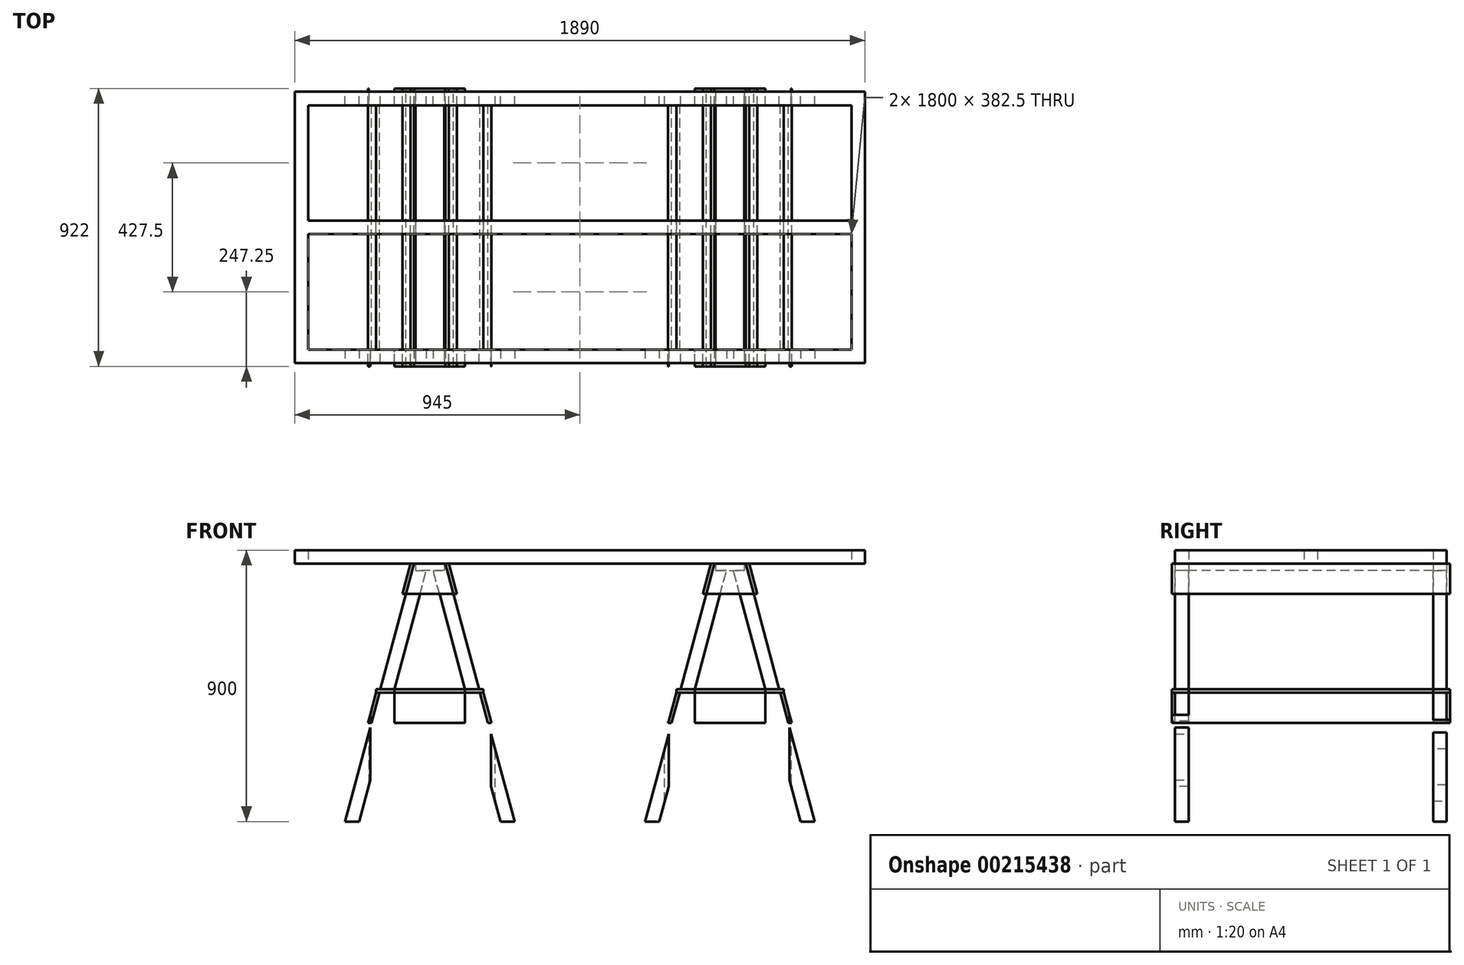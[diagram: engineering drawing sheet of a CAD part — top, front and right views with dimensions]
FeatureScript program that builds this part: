
annotation { "Feature Type Name" : "Feature", "Feature Type Description" : "" }
export const myFeature = defineFeature(function(context is Context, id is Id, definition is map)
    precondition{}
    {
        {
            var Q0;
            Q0=qCreatedBy(makeId("Top.planeOp"),FACE);
            var sketch = newSketch(context, id + "F0", { "sketchPlane" : qUnion([Q0])});
            skLineSegment(sketch, "E0.bottom", {"start": v(945, -450) * mm, "end": v(-945, -450) * mm});
            skLineSegment(sketch, "E0.top", {"start": v(945, 450) * mm, "end": v(-945, 450) * mm});
            skLineSegment(sketch, "E0.left", {"start": v(945, -450) * mm, "end": v(945, 450) * mm});
            skLineSegment(sketch, "E0.right", {"start": v(-945, -450) * mm, "end": v(-945, 450) * mm});
            skLineSegment(sketch, "E1.0", {"start": v(900, 405) * mm, "end": v(-900, 405) * mm});
            skLineSegment(sketch, "E1.1", {"start": v(900, -405) * mm, "end": v(900, 405) * mm});
            skLineSegment(sketch, "E1.2", {"start": v(900, -405) * mm, "end": v(-900, -405) * mm});
            skLineSegment(sketch, "E1.3", {"start": v(-900, -405) * mm, "end": v(-900, 405) * mm});
            skLineSegment(sketch, "E2.bottom", {"start": v(900, -22.5) * mm, "end": v(-900, -22.5) * mm});
            skLineSegment(sketch, "E2.top", {"start": v(900, 22.5) * mm, "end": v(-900, 22.5) * mm});
            skLineSegment(sketch, "E2.left", {"start": v(900, -22.5) * mm, "end": v(900, 22.5) * mm});
            skLineSegment(sketch, "E2.right", {"start": v(-900, -22.5) * mm, "end": v(-900, 22.5) * mm});
            skLineSegment(sketch, "E3.bottom", {"start": v(-320, 405) * mm, "end": v(-275, 405) * mm});
            skLineSegment(sketch, "E3.top", {"start": v(-320, -405) * mm, "end": v(-275, -405) * mm});
            skLineSegment(sketch, "E3.left", {"start": v(-320, 405) * mm, "end": v(-320, -405) * mm});
            skLineSegment(sketch, "E3.right", {"start": v(-275, 405) * mm, "end": v(-275, -405) * mm});
            skLineSegment(sketch, "E4.bottom", {"start": v(275, 405) * mm, "end": v(320, 405) * mm});
            skLineSegment(sketch, "E4.top", {"start": v(275, -405) * mm, "end": v(320, -405) * mm});
            skLineSegment(sketch, "E4.left", {"start": v(275, 405) * mm, "end": v(275, -405) * mm});
            skLineSegment(sketch, "E4.right", {"start": v(320, 405) * mm, "end": v(320, -405) * mm});
            skLineSegment(sketch, "E5", {"start": v(-297.5, 556.74) * mm, "end": v(-297.5, -663.13) * mm, "construction": true});
            skLineSegment(sketch, "E6", {"start": v(297.5, 521.89) * mm, "end": v(297.5, -577.16) * mm, "construction": true});
            skLineSegment(sketch, "E7", {"start": v(0, 0) * mm, "end": v(-1247.86, 0) * mm, "construction": true});
            skLineSegment(sketch, "E8", {"start": v(0, 0) * mm, "end": v(0, -826.24) * mm, "construction": true});
            skPoint(sketch, "E8.endSnap0", {"position": v(0, -405) * mm});
            skSolve(sketch);
        }
        {
            var Q0;
            Q0 = qSketchRegion(id + "F0", true);
            var Q1;
            {var subQ5=sQuery(id+"F0.wireOp",EDGE,"E3.bottom");Q1=makeQuery(id+"F0.imprint","IMPRINT",FACE,{"disambiguationData":[TD([[makeQuery(id+"F0.imprint","IMPRINT",EDGE,{"derivedFrom":subQ5}),-1.0]])]});}
            var Q2;
            {var subQ0=sQuery(id+"F0.wireOp",EDGE,"E2.right");Q2=makeQuery(id+"F0.imprint","IMPRINT",FACE,{"disambiguationData":[TD([[makeQuery(id+"F0.imprint","IMPRINT",EDGE,{"derivedFrom":subQ0}),-1.0]])]});}
            var Q3;
            {var subQ0=sQuery(id+"F0.wireOp",EDGE,"E3.right");var subQ1=sQuery(id+"F0.wireOp",EDGE,"E2.bottom");var subQ2=makeQuery(id+"F0.imprint","INTERSECT",VERTEX,{"derivedFrom":[subQ1,subQ0]});Q3=makeQuery(id+"F0.imprint","IMPRINT",FACE,{"disambiguationData":[TD([[makeQuery(id+"F0.imprint","IMPRINT",EDGE,{"disambiguationData":[TD([[subQ2,-1.0]])],"derivedFrom":subQ1}),-1.0]])]});}
            var Q4;
            {var subQ5=sQuery(id+"F0.wireOp",EDGE,"E3.top");Q4=makeQuery(id+"F0.imprint","IMPRINT",FACE,{"disambiguationData":[TD([[makeQuery(id+"F0.imprint","IMPRINT",EDGE,{"derivedFrom":subQ5}),1.0]])]});}
            var Q5;
            {var subQ0=sQuery(id+"F0.wireOp",EDGE,"EqetSjWE-wR77-RckO-4Gww-h4ygaoZgAjXq.right");var subQ1=sQuery(id+"F0.wireOp",EDGE,"E2.bottom");var subQ2=makeQuery(id+"F0.imprint","INTERSECT",VERTEX,{"derivedFrom":[subQ1,subQ0]});Q5=makeQuery(id+"F0.imprint","IMPRINT",FACE,{"disambiguationData":[TD([[makeQuery(id+"F0.imprint","IMPRINT",EDGE,{"disambiguationData":[TD([[subQ2,-1.0]])],"derivedFrom":subQ1}),-1.0]])]});}
            var Q6;
            {var subQ5=sQuery(id+"F0.wireOp",EDGE,"EqetSjWE-wR77-RckO-4Gww-h4ygaoZgAjXq.top");Q6=makeQuery(id+"F0.imprint","IMPRINT",FACE,{"disambiguationData":[TD([[makeQuery(id+"F0.imprint","IMPRINT",EDGE,{"derivedFrom":subQ5}),1.0]])]});}
            var Q7;
            {var subQ0=sQuery(id+"F0.wireOp",EDGE,"E4.left");var subQ1=sQuery(id+"F0.wireOp",EDGE,"E2.bottom");var subQ2=makeQuery(id+"F0.imprint","INTERSECT",VERTEX,{"derivedFrom":[subQ1,subQ0]});Q7=makeQuery(id+"F0.imprint","IMPRINT",FACE,{"disambiguationData":[TD([[makeQuery(id+"F0.imprint","IMPRINT",EDGE,{"disambiguationData":[TD([[subQ2,-1.0]])],"derivedFrom":subQ1}),-1.0]])]});}
            var Q8;
            {var subQ5=sQuery(id+"F0.wireOp",EDGE,"E4.bottom");Q8=makeQuery(id+"F0.imprint","IMPRINT",FACE,{"disambiguationData":[TD([[makeQuery(id+"F0.imprint","IMPRINT",EDGE,{"derivedFrom":subQ5}),-1.0]])]});}
            var Q9;
            {var subQ0=sQuery(id+"F0.wireOp",EDGE,"E2.left");Q9=makeQuery(id+"F0.imprint","IMPRINT",FACE,{"disambiguationData":[TD([[makeQuery(id+"F0.imprint","IMPRINT",EDGE,{"derivedFrom":subQ0}),1.0]])]});}
            var Q10;
            {var subQ5=sQuery(id+"F0.wireOp",EDGE,"E4.top");Q10=makeQuery(id+"F0.imprint","IMPRINT",FACE,{"disambiguationData":[TD([[makeQuery(id+"F0.imprint","IMPRINT",EDGE,{"derivedFrom":subQ5}),1.0]])]});}
            var Q11;
            {var subQ0=sQuery(id+"F0.wireOp",EDGE,"E4.right");var subQ1=sQuery(id+"F0.wireOp",EDGE,"E2.bottom");var subQ2=makeQuery(id+"F0.imprint","INTERSECT",VERTEX,{"derivedFrom":[subQ1,subQ0]});Q11=makeQuery(id+"F0.imprint","IMPRINT",FACE,{"disambiguationData":[TD([[makeQuery(id+"F0.imprint","IMPRINT",EDGE,{"disambiguationData":[TD([[subQ2,-1.0]])],"derivedFrom":subQ1}),-1.0]])]});}
            var Q12;
            {var subQ5=sQuery(id+"F0.wireOp",EDGE,"EqetSjWE-wR77-RckO-4Gww-h4ygaoZgAjXq.bottom");Q12=makeQuery(id+"F0.imprint","IMPRINT",FACE,{"disambiguationData":[TD([[makeQuery(id+"F0.imprint","IMPRINT",EDGE,{"derivedFrom":subQ5}),-1.0]])]});}
            var Q13;
            {var subQ0=sQuery(id+"F0.wireOp",EDGE,"EqetSjWE-wR77-RckO-4Gww-h4ygaoZgAjXq.left");var subQ1=sQuery(id+"F0.wireOp",EDGE,"E2.bottom");var subQ2=makeQuery(id+"F0.imprint","INTERSECT",VERTEX,{"derivedFrom":[subQ1,subQ0]});Q13=makeQuery(id+"F0.imprint","IMPRINT",FACE,{"disambiguationData":[TD([[makeQuery(id+"F0.imprint","IMPRINT",EDGE,{"disambiguationData":[TD([[subQ2,-1.0]])],"derivedFrom":subQ1}),-1.0]])]});}
            extrude(context, id + "F1", {"entities" : qUnion([Q0, Q1, Q2, Q3, Q4, Q5, Q6, Q7, Q8, Q9, Q10, Q11, Q12, Q13]), "depth" : 45 * mm});
        }
        {
            var Q0;
            Q0=makeQuery(id+"F1.opExtrude","SWEPT_FACE",FACE,{"disambiguationData":[OSD([sQuery(id+"F0.wireOp",EDGE,"E0.bottom")])]});
            var sketch = newSketch(context, id + "F2", { "sketchPlane" : qUnion([Q0])});
            skLineSegment(sketch, "E9.bottom", {"start": v(-545, 0) * mm, "end": v(-450, 0) * mm});
            skLineSegment(sketch, "E9.top", {"start": v(-545, -22) * mm, "end": v(-450, -22) * mm});
            skLineSegment(sketch, "E9.left", {"start": v(-545, 0) * mm, "end": v(-545, -22) * mm});
            skLineSegment(sketch, "E9.right", {"start": v(-450, 0) * mm, "end": v(-450, -22) * mm});
            skPoint(sketch, "E10.endSnap0", {"position": v(-297.5, 22.5) * mm});
            skSolve(sketch);
        }
        {
            var Q0;
            Q0 = qSketchRegion(id + "F2", true);
            var Q1;
            Q1=makeQuery(id+"F1.opExtrude","SWEPT_FACE",FACE,{"disambiguationData":[OSD([sQuery(id+"F0.wireOp",EDGE,"E0.top")])]});
            extrude(context, id + "F3", {"entities" : qUnion([Q0]), "endBound" : BoundingType.UP_TO_SURFACE, "oppositeDirection" : true, "endBoundEntityFace" : qUnion([Q1]), "depth" : 25 * mm});
        }
        {
            var Q0;
            Q0=makeQuery(id+"F3.opExtrude","CAP_FACE",FACE,{"disambiguationData":[OSD([sQuery(id+"F2.wireOp",EDGE,"E9.bottom"),sQuery(id+"F2.wireOp",EDGE,"E9.top"),sQuery(id+"F2.wireOp",EDGE,"E9.left"),sQuery(id+"F2.wireOp",EDGE,"E9.right")])],"isStart":true});
            var sketch = newSketch(context, id + "F4", { "sketchPlane" : qUnion([Q0])});
            skLineSegment(sketch, "E11", {"start": v(-497.5, 134.53) * mm, "end": v(-497.5, -899.08) * mm, "construction": true});
            skPoint(sketch, "E11.startSnap0", {"position": v(-497.5, -22) * mm});
            skLineSegment(sketch, "E12", {"start": v(-549.48, 0) * mm, "end": v(-778.58, -855) * mm});
            skLineSegment(sketch, "E13", {"start": v(-778.58, -855) * mm, "end": v(-732, -855) * mm});
            skLineSegment(sketch, "E14", {"start": v(-732, -855) * mm, "end": v(-508.8, -22) * mm});
            skLineSegment(sketch, "E15", {"start": v(-508.8, -22) * mm, "end": v(-545, -22) * mm});
            skLineSegment(sketch, "E16", {"start": v(-545, -22) * mm, "end": v(-545, 0) * mm});
            skLineSegment(sketch, "E17.MirrorCS", {"start": v(-450, -22) * mm, "end": v(-450, 0) * mm});
            skLineSegment(sketch, "E18.MirrorCS", {"start": v(-486.2, -22) * mm, "end": v(-450, -22) * mm});
            skLineSegment(sketch, "E19.MirrorCS", {"start": v(-216.42, -855) * mm, "end": v(-263, -855) * mm});
            skLineSegment(sketch, "E20.MirrorCS", {"start": v(-445.52, 0) * mm, "end": v(-216.42, -855) * mm});
            skLineSegment(sketch, "E21.MirrorCS", {"start": v(-263, -855) * mm, "end": v(-486.2, -22) * mm});
            skLineSegment(sketch, "E22", {"start": v(-545, 0) * mm, "end": v(-549.48, 0) * mm});
            skLineSegment(sketch, "E23", {"start": v(-450, 0) * mm, "end": v(-445.52, 0) * mm});
            skPoint(sketch, "E24.orphan", {"position": v(-545, 16.74) * mm});
            skPoint(sketch, "E25.orphan", {"position": v(-450, 16.74) * mm});
            skSolve(sketch);
        }
        {
            var Q0;
            Q0 = qSketchRegion(id + "F4", true);
            extrude(context, id + "F5", {"entities" : qUnion([Q0]), "oppositeDirection" : true, "depth" : 45 * mm});
        }
        {
            var Q0;
            Q0=makeQuery(id+"F5.opExtrude","CAP_FACE",FACE,{"disambiguationData":[OSD([sQuery(id+"F4.wireOp",EDGE,"E12"),sQuery(id+"F4.wireOp",EDGE,"E13"),sQuery(id+"F4.wireOp",EDGE,"E14"),sQuery(id+"F4.wireOp",EDGE,"E15"),sQuery(id+"F4.wireOp",EDGE,"E16"),sQuery(id+"F4.wireOp",EDGE,"E22")])],"isStart":true});
            var sketch = newSketch(context, id + "F6", { "sketchPlane" : qUnion([Q0])});
            skLineSegment(sketch, "E26", {"start": v(-664.03, -427.5) * mm, "end": v(-330.97, -427.5) * mm});
            skPoint(sketch, "E26.endSnap0", {"position": v(-664.03, -427.5) * mm});
            skLineSegment(sketch, "E27", {"start": v(-330.97, -427.5) * mm, "end": v(-304.17, -527.5) * mm});
            skLineSegment(sketch, "E28", {"start": v(-304.17, -527.5) * mm, "end": v(-690.83, -527.5) * mm});
            skLineSegment(sketch, "E29", {"start": v(-690.83, -527.5) * mm, "end": v(-664.03, -427.5) * mm});
            skLineSegment(sketch, "E30", {"start": v(-549.48, 0) * mm, "end": v(-445.52, 0) * mm});
            skLineSegment(sketch, "E31", {"start": v(-445.52, 0) * mm, "end": v(-418.72, -100) * mm});
            skLineSegment(sketch, "E32", {"start": v(-418.72, -100) * mm, "end": v(-576.28, -100) * mm});
            skLineSegment(sketch, "E33", {"start": v(-576.28, -100) * mm, "end": v(-549.48, 0) * mm});
            skSolve(sketch);
        }
        {
            var Q0;
            Q0 = qSketchRegion(id + "F6", true);
            extrude(context, id + "F7", {"entities" : qUnion([Q0]), "depth" : 11 * mm});
        }
        {
            var Q0;
            Q0=makeQuery(id+"F5.opExtrude","SWEPT_BODY",BODY,{"disambiguationData":[OSD([sQuery(id+"F4.wireOp",EDGE,"E12"),sQuery(id+"F4.wireOp",EDGE,"E13"),sQuery(id+"F4.wireOp",EDGE,"E14"),sQuery(id+"F4.wireOp",EDGE,"E15"),sQuery(id+"F4.wireOp",EDGE,"E16"),sQuery(id+"F4.wireOp",EDGE,"E22")])]});
            var Q1;
            Q1=makeQuery(id+"F5.opExtrude","SWEPT_BODY",BODY,{"disambiguationData":[OSD([sQuery(id+"F4.wireOp",EDGE,"E17.MirrorCS"),sQuery(id+"F4.wireOp",EDGE,"E18.MirrorCS"),sQuery(id+"F4.wireOp",EDGE,"E19.MirrorCS"),sQuery(id+"F4.wireOp",EDGE,"E20.MirrorCS"),sQuery(id+"F4.wireOp",EDGE,"E21.MirrorCS"),sQuery(id+"F4.wireOp",EDGE,"E23")])]});
            var Q2;
            Q2=makeQuery(id+"F7.opExtrude","SWEPT_BODY",BODY,{"disambiguationData":[OSD([sQuery(id+"F6.wireOp",EDGE,"E26"),sQuery(id+"F6.wireOp",EDGE,"E27"),sQuery(id+"F6.wireOp",EDGE,"E28"),sQuery(id+"F6.wireOp",EDGE,"E29")])]});
            var Q3;
            Q3=makeQuery(id+"F7.opExtrude","SWEPT_BODY",BODY,{"disambiguationData":[OSD([sQuery(id+"F6.wireOp",EDGE,"E30"),sQuery(id+"F6.wireOp",EDGE,"E31"),sQuery(id+"F6.wireOp",EDGE,"E32"),sQuery(id+"F6.wireOp",EDGE,"E33")])]});
            var Q4;
            Q4=qCreatedBy(makeId("Front.planeOp"),FACE);
            mirror(context, id + "F8", {"entities" : qUnion([Q0, Q1, Q2, Q3]), "mirrorPlane" : qUnion([Q4])});
        }
        {
            var Q0;
            Q0=makeQuery(id+"F8.opPattern","COPY",FACE,{"derivedFrom":makeQuery(id+"F7.opExtrude","CAP_FACE",FACE,{"disambiguationData":[OSD([sQuery(id+"F6.wireOp",EDGE,"E30"),sQuery(id+"F6.wireOp",EDGE,"E31"),sQuery(id+"F6.wireOp",EDGE,"E32"),sQuery(id+"F6.wireOp",EDGE,"E33")])],"isStart":false}),"instanceName":"1"});
            var sketch = newSketch(context, id + "F9", { "sketchPlane" : qUnion([Q0])});
            skLineSegment(sketch, "E34", {"start": v(445.52, 0) * mm, "end": v(434.13, 0) * mm});
            skLineSegment(sketch, "E35", {"start": v(434.13, 0) * mm, "end": v(407.33, -100) * mm});
            skLineSegment(sketch, "E36", {"start": v(407.33, -100) * mm, "end": v(418.72, -100) * mm});
            skLineSegment(sketch, "E37", {"start": v(418.72, -100) * mm, "end": v(445.52, 0) * mm});
            skLineSegment(sketch, "E38", {"start": v(549.48, 0) * mm, "end": v(560.87, 0) * mm});
            skLineSegment(sketch, "E39", {"start": v(560.87, 0) * mm, "end": v(587.67, -100) * mm});
            skLineSegment(sketch, "E40", {"start": v(587.67, -100) * mm, "end": v(576.28, -100) * mm});
            skLineSegment(sketch, "E41", {"start": v(576.28, -100) * mm, "end": v(549.48, 0) * mm});
            skLineSegment(sketch, "E42", {"start": v(330.97, -427.5) * mm, "end": v(319.58, -427.5) * mm});
            skLineSegment(sketch, "E43", {"start": v(319.58, -427.5) * mm, "end": v(292.78, -527.5) * mm});
            skLineSegment(sketch, "E44", {"start": v(292.78, -527.5) * mm, "end": v(304.17, -527.5) * mm});
            skLineSegment(sketch, "E45", {"start": v(304.17, -527.5) * mm, "end": v(330.97, -427.5) * mm});
            skLineSegment(sketch, "E46", {"start": v(664.03, -427.5) * mm, "end": v(675.42, -427.5) * mm});
            skLineSegment(sketch, "E47", {"start": v(675.42, -427.5) * mm, "end": v(702.22, -527.5) * mm});
            skLineSegment(sketch, "E48", {"start": v(702.22, -527.5) * mm, "end": v(690.83, -527.5) * mm});
            skLineSegment(sketch, "E49", {"start": v(690.83, -527.5) * mm, "end": v(664.03, -427.5) * mm});
            skSolve(sketch);
        }
        {
            var Q0;
            Q0 = qSketchRegion(id + "F9", true);
            var Q1;
            Q1=makeQuery(id+"F7.opExtrude","CAP_FACE",FACE,{"disambiguationData":[OSD([sQuery(id+"F6.wireOp",EDGE,"E30"),sQuery(id+"F6.wireOp",EDGE,"E31"),sQuery(id+"F6.wireOp",EDGE,"E32"),sQuery(id+"F6.wireOp",EDGE,"E33")])],"isStart":false});
            extrude(context, id + "F10", {"entities" : qUnion([Q0]), "endBound" : BoundingType.UP_TO_SURFACE, "oppositeDirection" : true, "endBoundEntityFace" : qUnion([Q1]), "depth" : 25 * mm});
        }
        {
            var Q0;
            Q0=makeQuery(id+"F10.opExtrude","SWEPT_FACE",FACE,{"disambiguationData":[OSD([sQuery(id+"F9.wireOp",EDGE,"E46")])]});
            var sketch = newSketch(context, id + "F11", { "sketchPlane" : qUnion([Q0])});
            skLineSegment(sketch, "E50.bottom", {"start": v(-675.42, 461) * mm, "end": v(-319.58, 461) * mm});
            skLineSegment(sketch, "E50.top", {"start": v(-675.42, -461) * mm, "end": v(-319.58, -461) * mm});
            skLineSegment(sketch, "E50.left", {"start": v(-675.42, 461) * mm, "end": v(-675.42, -461) * mm});
            skLineSegment(sketch, "E50.right", {"start": v(-319.58, 461) * mm, "end": v(-319.58, -461) * mm});
            skSolve(sketch);
        }
        {
            var Q0;
            Q0 = qSketchRegion(id + "F11", true);
            extrude(context, id + "F12", {"entities" : qUnion([Q0]), "depth" : 11 * mm});
        }
        {
            var Q0;
            Q0=makeQuery(id+"F5.opExtrude","SWEPT_BODY",BODY,{"disambiguationData":[OSD([sQuery(id+"F4.wireOp",EDGE,"E12"),sQuery(id+"F4.wireOp",EDGE,"E13"),sQuery(id+"F4.wireOp",EDGE,"E14"),sQuery(id+"F4.wireOp",EDGE,"E15"),sQuery(id+"F4.wireOp",EDGE,"E16"),sQuery(id+"F4.wireOp",EDGE,"E22")])]});
            var Q1;
            Q1=makeQuery(id+"F5.opExtrude","SWEPT_BODY",BODY,{"disambiguationData":[OSD([sQuery(id+"F4.wireOp",EDGE,"E17.MirrorCS"),sQuery(id+"F4.wireOp",EDGE,"E18.MirrorCS"),sQuery(id+"F4.wireOp",EDGE,"E19.MirrorCS"),sQuery(id+"F4.wireOp",EDGE,"E20.MirrorCS"),sQuery(id+"F4.wireOp",EDGE,"E21.MirrorCS"),sQuery(id+"F4.wireOp",EDGE,"E23")])]});
            var Q2;
            Q2=makeQuery(id+"F8.opPattern","COPY",BODY,{"derivedFrom":makeQuery(id+"F5.opExtrude","SWEPT_BODY",BODY,{"disambiguationData":[OSD([sQuery(id+"F4.wireOp",EDGE,"E12"),sQuery(id+"F4.wireOp",EDGE,"E13"),sQuery(id+"F4.wireOp",EDGE,"E14"),sQuery(id+"F4.wireOp",EDGE,"E15"),sQuery(id+"F4.wireOp",EDGE,"E16"),sQuery(id+"F4.wireOp",EDGE,"E22")])]}),"instanceName":"1"});
            var Q3;
            Q3=makeQuery(id+"F8.opPattern","COPY",BODY,{"derivedFrom":makeQuery(id+"F5.opExtrude","SWEPT_BODY",BODY,{"disambiguationData":[OSD([sQuery(id+"F4.wireOp",EDGE,"E17.MirrorCS"),sQuery(id+"F4.wireOp",EDGE,"E18.MirrorCS"),sQuery(id+"F4.wireOp",EDGE,"E19.MirrorCS"),sQuery(id+"F4.wireOp",EDGE,"E20.MirrorCS"),sQuery(id+"F4.wireOp",EDGE,"E21.MirrorCS"),sQuery(id+"F4.wireOp",EDGE,"E23")])]}),"instanceName":"1"});
            var Q4;
            Q4=makeQuery(id+"F12.opExtrude","SWEPT_BODY",BODY,{"disambiguationData":[OSD([sQuery(id+"F11.wireOp",EDGE,"E50.bottom"),sQuery(id+"F11.wireOp",EDGE,"E50.top"),sQuery(id+"F11.wireOp",EDGE,"E50.left"),sQuery(id+"F11.wireOp",EDGE,"E50.right")])]});
            booleanBodies(context, id + "F13", {"operationType" : BooleanOperationType.SUBTRACTION, "tools" : qUnion([Q0, Q1, Q2, Q3]), "targets" : qUnion([Q4]), "keepTools" : true});
        }
        {
            var Q0;
            Q0=makeQuery(id+"F12.opExtrude","CAP_FACE",FACE,{"disambiguationData":[OSD([sQuery(id+"F11.wireOp",EDGE,"E50.bottom"),sQuery(id+"F11.wireOp",EDGE,"E50.top"),sQuery(id+"F11.wireOp",EDGE,"E50.left"),sQuery(id+"F11.wireOp",EDGE,"E50.right")])],"isStart":false});
            var sketch = newSketch(context, id + "F14", { "sketchPlane" : qUnion([Q0])});
            skLineSegment(sketch, "E51.bottom", {"start": v(-614.5, -405) * mm, "end": v(-695, -405) * mm});
            skLineSegment(sketch, "E51.top", {"start": v(-614.5, -489.97) * mm, "end": v(-695, -489.97) * mm});
            skLineSegment(sketch, "E51.left", {"start": v(-614.5, -405) * mm, "end": v(-614.5, -489.97) * mm});
            skLineSegment(sketch, "E51.right", {"start": v(-695, -405) * mm, "end": v(-695, -489.97) * mm});
            skLineSegment(sketch, "E52.bottom", {"start": v(-380.5, -405) * mm, "end": v(-294.35, -405) * mm});
            skLineSegment(sketch, "E52.top", {"start": v(-380.5, -513.2) * mm, "end": v(-294.35, -513.2) * mm});
            skLineSegment(sketch, "E52.left", {"start": v(-380.5, -405) * mm, "end": v(-380.5, -513.2) * mm});
            skLineSegment(sketch, "E52.right", {"start": v(-294.35, -405) * mm, "end": v(-294.35, -513.2) * mm});
            skLineSegment(sketch, "E53.bottom", {"start": v(-614.5, 405) * mm, "end": v(-699.49, 405) * mm});
            skLineSegment(sketch, "E53.top", {"start": v(-614.5, 482.33) * mm, "end": v(-699.49, 482.33) * mm});
            skLineSegment(sketch, "E53.left", {"start": v(-614.5, 405) * mm, "end": v(-614.5, 482.33) * mm});
            skLineSegment(sketch, "E53.right", {"start": v(-699.49, 405) * mm, "end": v(-699.49, 482.33) * mm});
            skLineSegment(sketch, "E54.bottom", {"start": v(-380.5, 405) * mm, "end": v(-281.11, 405) * mm});
            skLineSegment(sketch, "E54.top", {"start": v(-380.5, 507.07) * mm, "end": v(-281.11, 507.07) * mm});
            skLineSegment(sketch, "E54.left", {"start": v(-380.5, 405) * mm, "end": v(-380.5, 507.07) * mm});
            skLineSegment(sketch, "E54.right", {"start": v(-281.11, 405) * mm, "end": v(-281.11, 507.07) * mm});
            skSolve(sketch);
        }
        {
            var Q0;
            Q0 = qSketchRegion(id + "F14", true);
            extrude(context, id + "F15", {"entities" : qUnion([Q0]), "operationType" : NewBodyOperationType.REMOVE, "endBound" : BoundingType.THROUGH_ALL, "oppositeDirection" : true, "depth" : 25 * mm});
        }
        {
            var Q0;
            Q0=makeQuery(id+"F5.opExtrude","SWEPT_BODY",BODY,{"disambiguationData":[OSD([sQuery(id+"F4.wireOp",EDGE,"E17.MirrorCS"),sQuery(id+"F4.wireOp",EDGE,"E18.MirrorCS"),sQuery(id+"F4.wireOp",EDGE,"E19.MirrorCS"),sQuery(id+"F4.wireOp",EDGE,"E20.MirrorCS"),sQuery(id+"F4.wireOp",EDGE,"E21.MirrorCS"),sQuery(id+"F4.wireOp",EDGE,"E23")])]});
            var Q1;
            Q1=makeQuery(id+"F5.opExtrude","SWEPT_BODY",BODY,{"disambiguationData":[OSD([sQuery(id+"F4.wireOp",EDGE,"E12"),sQuery(id+"F4.wireOp",EDGE,"E13"),sQuery(id+"F4.wireOp",EDGE,"E14"),sQuery(id+"F4.wireOp",EDGE,"E15"),sQuery(id+"F4.wireOp",EDGE,"E16"),sQuery(id+"F4.wireOp",EDGE,"E22")])]});
            var Q2;
            Q2=makeQuery(id+"F3.opExtrude","SWEPT_BODY",BODY,{"disambiguationData":[OSD([sQuery(id+"F2.wireOp",EDGE,"E9.bottom"),sQuery(id+"F2.wireOp",EDGE,"E9.top"),sQuery(id+"F2.wireOp",EDGE,"E9.left"),sQuery(id+"F2.wireOp",EDGE,"E9.right")])]});
            var Q3;
            Q3=makeQuery(id+"F8.opPattern","COPY",BODY,{"derivedFrom":makeQuery(id+"F7.opExtrude","SWEPT_BODY",BODY,{"disambiguationData":[OSD([sQuery(id+"F6.wireOp",EDGE,"E26"),sQuery(id+"F6.wireOp",EDGE,"E27"),sQuery(id+"F6.wireOp",EDGE,"E28"),sQuery(id+"F6.wireOp",EDGE,"E29")])]}),"instanceName":"1"});
            var Q4;
            Q4=makeQuery(id+"F8.opPattern","COPY",BODY,{"derivedFrom":makeQuery(id+"F5.opExtrude","SWEPT_BODY",BODY,{"disambiguationData":[OSD([sQuery(id+"F4.wireOp",EDGE,"E12"),sQuery(id+"F4.wireOp",EDGE,"E13"),sQuery(id+"F4.wireOp",EDGE,"E14"),sQuery(id+"F4.wireOp",EDGE,"E15"),sQuery(id+"F4.wireOp",EDGE,"E16"),sQuery(id+"F4.wireOp",EDGE,"E22")])]}),"instanceName":"1"});
            var Q5;
            Q5=makeQuery(id+"F8.opPattern","COPY",BODY,{"derivedFrom":makeQuery(id+"F5.opExtrude","SWEPT_BODY",BODY,{"disambiguationData":[OSD([sQuery(id+"F4.wireOp",EDGE,"E17.MirrorCS"),sQuery(id+"F4.wireOp",EDGE,"E18.MirrorCS"),sQuery(id+"F4.wireOp",EDGE,"E19.MirrorCS"),sQuery(id+"F4.wireOp",EDGE,"E20.MirrorCS"),sQuery(id+"F4.wireOp",EDGE,"E21.MirrorCS"),sQuery(id+"F4.wireOp",EDGE,"E23")])]}),"instanceName":"1"});
            var Q6;
            Q6=makeQuery(id+"F8.opPattern","COPY",BODY,{"derivedFrom":makeQuery(id+"F7.opExtrude","SWEPT_BODY",BODY,{"disambiguationData":[OSD([sQuery(id+"F6.wireOp",EDGE,"E30"),sQuery(id+"F6.wireOp",EDGE,"E31"),sQuery(id+"F6.wireOp",EDGE,"E32"),sQuery(id+"F6.wireOp",EDGE,"E33")])]}),"instanceName":"1"});
            var Q7;
            Q7=makeQuery(id+"Fm8UvPEJSUYjsHx_7.opExtrude","SWEPT_BODY",BODY,{"disambiguationData":[OSD([sQuery(id+"FUi2mpj8VYXKR7B_7.wireOp",EDGE,"jN1rMCq6-tiUL-lWp5-zI7q-xgaWdWhEiivF.bottom"),sQuery(id+"FUi2mpj8VYXKR7B_7.wireOp",EDGE,"jN1rMCq6-tiUL-lWp5-zI7q-xgaWdWhEiivF.top"),sQuery(id+"FUi2mpj8VYXKR7B_7.wireOp",EDGE,"jN1rMCq6-tiUL-lWp5-zI7q-xgaWdWhEiivF.left"),sQuery(id+"FUi2mpj8VYXKR7B_7.wireOp",EDGE,"jN1rMCq6-tiUL-lWp5-zI7q-xgaWdWhEiivF.right")])]});
            var Q8;
            Q8=makeQuery(id+"Fm8UvPEJSUYjsHx_7.opExtrude","SWEPT_BODY",BODY,{"disambiguationData":[OSD([sQuery(id+"FUi2mpj8VYXKR7B_7.wireOp",EDGE,"ZkVrbPfE-Oakc-2Pf6-dXQp-rwn4bSiBbaGY.bottom"),sQuery(id+"FUi2mpj8VYXKR7B_7.wireOp",EDGE,"ZkVrbPfE-Oakc-2Pf6-dXQp-rwn4bSiBbaGY.top"),sQuery(id+"FUi2mpj8VYXKR7B_7.wireOp",EDGE,"ZkVrbPfE-Oakc-2Pf6-dXQp-rwn4bSiBbaGY.left"),sQuery(id+"FUi2mpj8VYXKR7B_7.wireOp",EDGE,"ZkVrbPfE-Oakc-2Pf6-dXQp-rwn4bSiBbaGY.right")])]});
            var Q9;
            Q9=makeQuery(id+"Fm8UvPEJSUYjsHx_7.opExtrude","SWEPT_BODY",BODY,{"disambiguationData":[OSD([sQuery(id+"FUi2mpj8VYXKR7B_7.wireOp",EDGE,"efDMQflK-dC2w-odtw-3ici-RsCFYdMMO8eF.bottom"),sQuery(id+"FUi2mpj8VYXKR7B_7.wireOp",EDGE,"efDMQflK-dC2w-odtw-3ici-RsCFYdMMO8eF.top"),sQuery(id+"FUi2mpj8VYXKR7B_7.wireOp",EDGE,"efDMQflK-dC2w-odtw-3ici-RsCFYdMMO8eF.left"),sQuery(id+"FUi2mpj8VYXKR7B_7.wireOp",EDGE,"efDMQflK-dC2w-odtw-3ici-RsCFYdMMO8eF.right")])]});
            var Q10;
            Q10=makeQuery(id+"Fm8UvPEJSUYjsHx_7.opExtrude","SWEPT_BODY",BODY,{"disambiguationData":[OSD([sQuery(id+"FUi2mpj8VYXKR7B_7.wireOp",EDGE,"98YXF7q9-k07h-FTlE-4hYT-T7Ss0LfSZc2w.bottom"),sQuery(id+"FUi2mpj8VYXKR7B_7.wireOp",EDGE,"98YXF7q9-k07h-FTlE-4hYT-T7Ss0LfSZc2w.top"),sQuery(id+"FUi2mpj8VYXKR7B_7.wireOp",EDGE,"98YXF7q9-k07h-FTlE-4hYT-T7Ss0LfSZc2w.left"),sQuery(id+"FUi2mpj8VYXKR7B_7.wireOp",EDGE,"98YXF7q9-k07h-FTlE-4hYT-T7Ss0LfSZc2w.right")])]});
            var Q11;
            Q11=makeQuery(id+"F7.opExtrude","SWEPT_BODY",BODY,{"disambiguationData":[OSD([sQuery(id+"F6.wireOp",EDGE,"E26"),sQuery(id+"F6.wireOp",EDGE,"E27"),sQuery(id+"F6.wireOp",EDGE,"E28"),sQuery(id+"F6.wireOp",EDGE,"E29")])]});
            var Q12;
            Q12=makeQuery(id+"F7.opExtrude","SWEPT_BODY",BODY,{"disambiguationData":[OSD([sQuery(id+"F6.wireOp",EDGE,"E30"),sQuery(id+"F6.wireOp",EDGE,"E31"),sQuery(id+"F6.wireOp",EDGE,"E32"),sQuery(id+"F6.wireOp",EDGE,"E33")])]});
            var Q13;
            Q13=makeQuery(id+"F12.opExtrude","SWEPT_BODY",BODY,{"disambiguationData":[OSD([sQuery(id+"F11.wireOp",EDGE,"E50.bottom"),sQuery(id+"F11.wireOp",EDGE,"E50.top"),sQuery(id+"F11.wireOp",EDGE,"E50.left"),sQuery(id+"F11.wireOp",EDGE,"E50.right")])]});
            var Q14;
            Q14=makeQuery(id+"F10.opExtrude","SWEPT_BODY",BODY,{"disambiguationData":[OSD([sQuery(id+"F9.wireOp",EDGE,"E46"),sQuery(id+"F9.wireOp",EDGE,"E47"),sQuery(id+"F9.wireOp",EDGE,"E48"),sQuery(id+"F9.wireOp",EDGE,"E49")])]});
            var Q15;
            Q15=makeQuery(id+"F10.opExtrude","SWEPT_BODY",BODY,{"disambiguationData":[OSD([sQuery(id+"F9.wireOp",EDGE,"E42"),sQuery(id+"F9.wireOp",EDGE,"E43"),sQuery(id+"F9.wireOp",EDGE,"E44"),sQuery(id+"F9.wireOp",EDGE,"E45")])]});
            var Q16;
            Q16=makeQuery(id+"F10.opExtrude","SWEPT_BODY",BODY,{"disambiguationData":[OSD([sQuery(id+"F9.wireOp",EDGE,"E38"),sQuery(id+"F9.wireOp",EDGE,"E39"),sQuery(id+"F9.wireOp",EDGE,"E40"),sQuery(id+"F9.wireOp",EDGE,"E41")])]});
            var Q17;
            Q17=makeQuery(id+"F10.opExtrude","SWEPT_BODY",BODY,{"disambiguationData":[OSD([sQuery(id+"F9.wireOp",EDGE,"E34"),sQuery(id+"F9.wireOp",EDGE,"E35"),sQuery(id+"F9.wireOp",EDGE,"E36"),sQuery(id+"F9.wireOp",EDGE,"E37")])]});
            var Q18;
            Q18=qCreatedBy(makeId("Right.planeOp"),FACE);
            mirror(context, id + "F16", {"entities" : qUnion([Q0, Q1, Q2, Q3, Q4, Q5, Q6, Q7, Q8, Q9, Q10, Q11, Q12, Q13, Q14, Q15, Q16, Q17]), "mirrorPlane" : qUnion([Q18])});
        }
    });
